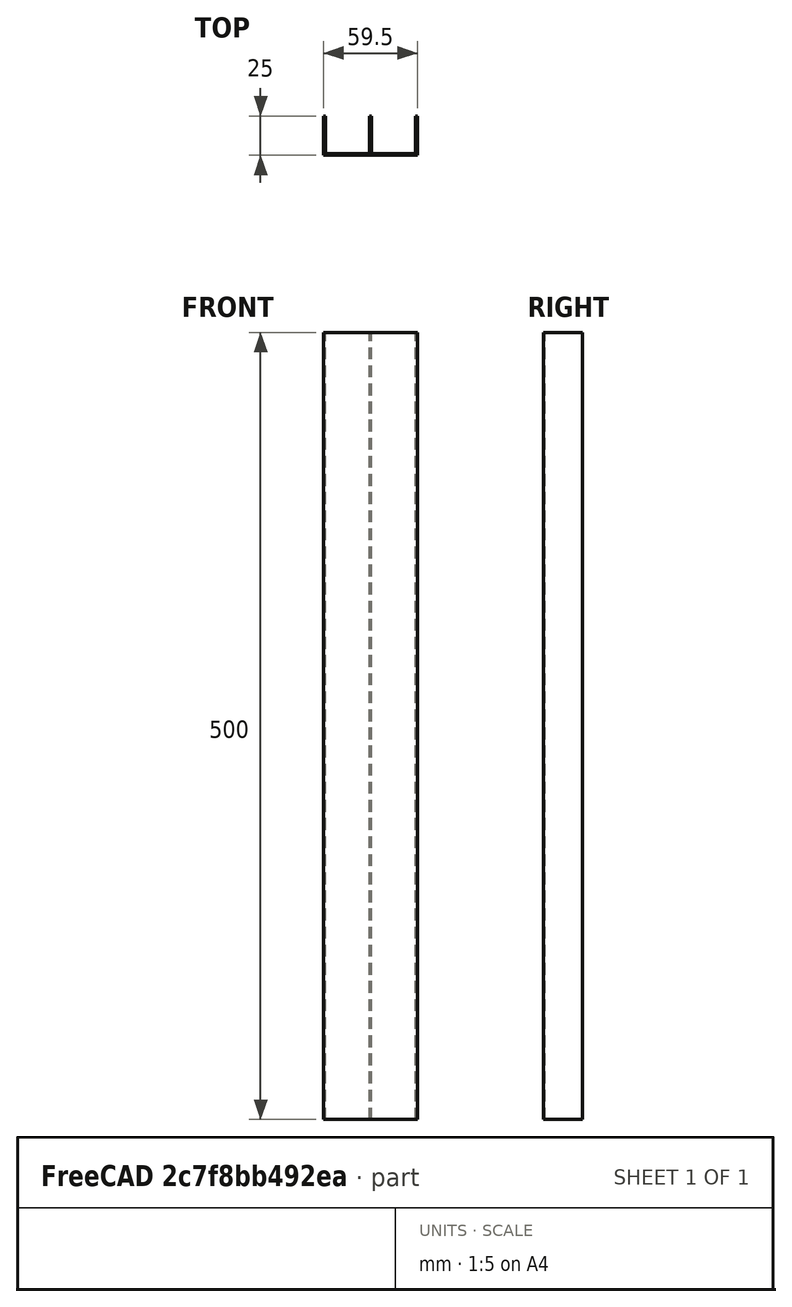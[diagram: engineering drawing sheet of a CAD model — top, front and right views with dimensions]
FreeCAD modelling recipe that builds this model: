
FCSTD DOCUMENT  (FreeCAD 0.20R29603 (Git))
Label: Trilho_RM025
License: All rights reserved
LicenseURL: http://en.wikipedia.org/wiki/All_rights_reserved
objects: Sketcher::SketchObject×1, PartDesign::Pad×1, PartDesign::Body×1, Spreadsheet::Sheet×1
note: 4 computed .brp shape members not serialized (recipe doc carries the construction recipe); baked Part::Feature solids carry a one-line shape summary decoded from their .brp

FEATURE [Sketcher::SketchObject] Sketch
  FullyConstrained = true
  MapMode = 5
  Support = -> [XY_Plane]
  expr: Constraints[24] = <<Params>>.width
  expr: Constraints[25] = <<Params>>.gap
  expr: Constraints[26] = <<Params>>.gap
  expr: Constraints[27] = <<Params>>.heigth
  expr: Constraints[30] = <<Params>>.thickness
  expr: Constraints[32] = <<Params>>.thickness
  sketch-geometry (12):
    g0: LineSegment StartX=-29.75 StartY=25 StartZ=0 EndX=-29.75 EndY=0 EndZ=0
    g1: LineSegment StartX=-29.75 StartY=0 StartZ=0 EndX=29.75 EndY=-1e-16 EndZ=0
    g2: LineSegment StartX=29.75 StartY=-1e-16 StartZ=0 EndX=29.75 EndY=25 EndZ=0
    g3: LineSegment StartX=29.75 StartY=25 StartZ=0 EndX=28.5833 EndY=25 EndZ=0
    g4: LineSegment StartX=28.5833 StartY=25 StartZ=0 EndX=28.5833 EndY=1.16667 EndZ=0
    g5: LineSegment StartX=28.5833 StartY=1.16667 StartZ=0 EndX=0.583333 EndY=1.16667 EndZ=0
    g6: LineSegment StartX=0.583333 StartY=1.16667 StartZ=0 EndX=0.583333 EndY=25 EndZ=0
    g7: LineSegment StartX=0.583333 StartY=25 StartZ=0 EndX=-0.583333 EndY=25 EndZ=0
    g8: LineSegment StartX=-0.583333 StartY=25 StartZ=0 EndX=-0.583333 EndY=1.16667 EndZ=0
    g9: LineSegment StartX=-0.583333 StartY=1.16667 StartZ=0 EndX=-28.5833 EndY=1.16667 EndZ=0
    g10: LineSegment StartX=-28.5833 StartY=1.16667 StartZ=0 EndX=-28.5833 EndY=25 EndZ=0
    g11: LineSegment StartX=-28.5833 StartY=25 StartZ=0 EndX=-29.75 EndY=25 EndZ=0
  constraints (35):
    c: PointOnObject(g0,g-1)
    c: Vertical(g0)
    c: Coincident(g1,g0)
    c: Vertical(g2)
    c: Horizontal(g3)
    c: Vertical(g4)
    c: Horizontal(g5)
    c: Vertical(g6)
    c: Vertical(g8)
    c: Horizontal(g9)
    c: Vertical(g10)
    c: Coincident(g11,g0)
    c: Coincident(g6,g7)
    c: Coincident(g4,g5)
    c: Coincident(g5,g6)
    c: Coincident(g4,g3)
    c: Coincident(g2,g3)
    c: Coincident(g1,g2)
    c: Coincident(g9,g10)
    c: Coincident(g9,g8)
    c: Coincident(g8,g7)
    c: Coincident(g11,g10)
    c: Horizontal(g11)
    c: Horizontal(g7)
    c: DistanceX(g0,g1) = 59.5
    c: DistanceX(g9,g8) = 28
    c: DistanceX(g5,g4) = 28
    c: DistanceY(g0,g0) = 25
    c: Horizontal(g0,g7)
    c: Horizontal(g7,g3)
    c: DistanceY(g1,g4) = 1.16667
    c: Horizontal(g8,g5)
    c: DistanceX(g0,g10) = 1.16667
    c: Equal(g11,g3)
    c: Symmetric(g0,g1,g-2)
FEATURE [PartDesign::Pad] Pad  label="Extrusion"
  Direction = (0,0,1)
  Length = 500
  Length2 = 10
  Profile = -> Sketch
  ReferenceAxis = -> Sketch [N_Axis]
  Type = 0
FEATURE [PartDesign::Body] Body
  Group = -> [Sketch,Pad]
  Origin = -> Origin
  Tip = -> Pad
FEATURE [Spreadsheet::Sheet] Spreadsheet  label="Params"
  cells = A1=length; B1(length)=500; A2=width; B2(width)=59.5; A3=heigth; B3(heigth)=25; A4=gap; B4(gap)=28; A5=thickness; B5(thickness)==(B2 - 2 * B4) / 3
